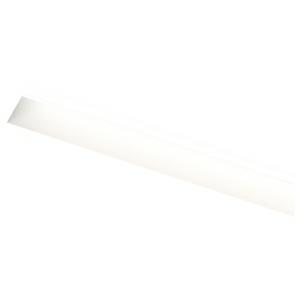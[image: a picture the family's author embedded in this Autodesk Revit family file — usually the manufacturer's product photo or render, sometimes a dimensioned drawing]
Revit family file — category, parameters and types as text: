
# Revit family: groove_l_2000_rl_led_37w_3000k_2386lm_cri80_130-0590_fc84
name_source: partatom
category: Leuchten
revit_build: Autodesk Revit 2016 (Build: 20190508_0715(x64)
units: mm (PartAtom-declared; Revit-internal decimal feet)

## family parameters
Basisbauteil = Fläche
Beim Laden mit Abzugskörper schneiden = Nein
Bemaßung runder Anschluss = Durchmesser verwenden
Gemeinsam genutzt = Nein
Lichtquelle = Nein
Raumberechnungspunkt = Nein
Teiletyp = Normal

## types (1)
- 130-0590- (7 x LED, 710 lm, 5.1 W, 3000K)
    Beschreibung = The rimless luminaire GROOVE from the familiy GROOVE consists of aluminum-extruded profile. Charming SOFT-EDGE design ensure unparalleled styling. The ballast is integrated and allows for an operation with 220-240V (50.60Hz). GROOVE (# 130-0590) ist not dimmable (on/off). The luminaire with direct illumination and corresponds to protection class SK1 at IP20.
    CIE Flux Codes = 59 87 97 100 49
    Color Rendering = 1B/80…89
    Color Temperature = 3000K
    Height = 0 mm  [stored 0 ft]
    Hersteller = Prolicht
    Lamp Light Flux = 710 lm
    Lamp Power = 5.1 W
    Lamp count = 7
    Lampe = 7 x LED
    Length = 2000 mm  [stored 6.56168 ft]
    Luminous efficacy = 67 lm/W
    ModVariant = Nein
    Modell = 130-0590
    Mounting Place = Ceiling
    Mounting Type = Recessed
    Number of Poles = 1
    OnlyDefault = Ja
    Power Factor = 1
    Product Name = GROOVE L=2000 RL LED 37W 3000K 2386lm CRI80
    Product group = Trimless recessed profile lights
    ProductGroupID = 413
    Protection Class = Protection class
    Protection Degree = Degree of protection
    RLX_Detail_Level = 1
    RlxData = <blob elided: 135553 chars, md5=8286ed10>
    Scheinlast = 36 VA
    Socket = socket
    Standby Power = 0 W
    System Light Flux = 2397 lm
    System Power = 36 W
    Typenbild = 130-0590.jpg
    URL = http://relux.com
    VarID = 130-0590-
    Voltage = 0 V
    Vorgabe-Ansicht = 1800 mm
    Weight = 0.00 kg
    Width = 75 mm

note: [stored X ft] marks values corroborated as IEEE doubles in the binary element streams (Revit-internal decimal feet)

## geometry (parser evidence)
native form markers: Blend x4, Sweep x9
no freeform markers — native parametric forms only
